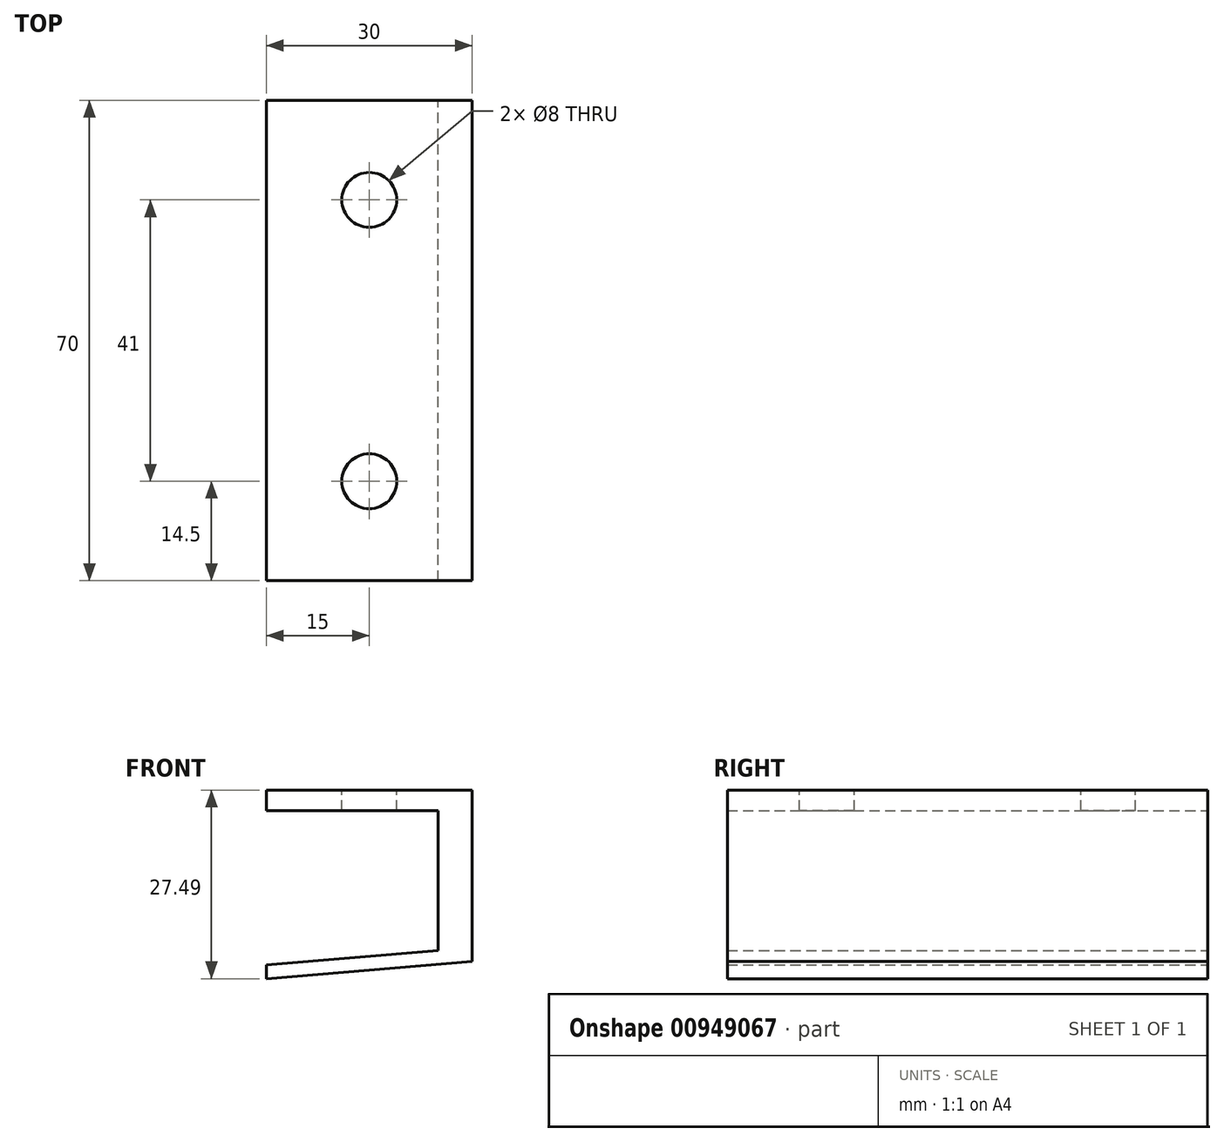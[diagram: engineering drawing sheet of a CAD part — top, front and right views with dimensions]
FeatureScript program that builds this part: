
annotation { "Feature Type Name" : "Feature", "Feature Type Description" : "" }
export const myFeature = defineFeature(function(context is Context, id is Id, definition is map)
    precondition{}
    {
        {
            var Q0;
            Q0=qCreatedBy(makeId("Front.planeOp"),FACE);
            var sketch = newSketch(context, id + "F0", { "sketchPlane" : qUnion([Q0])});
            skLineSegment(sketch, "E0", {"start": v(0, 0) * mm, "end": v(0, 3) * mm});
            skLineSegment(sketch, "E1", {"start": v(0, 3) * mm, "end": v(30, 3) * mm});
            skLineSegment(sketch, "E2", {"start": v(30, 3) * mm, "end": v(30, -22) * mm});
            skLineSegment(sketch, "E3", {"start": v(0, 0) * mm, "end": v(25, 0) * mm});
            skLineSegment(sketch, "E4", {"start": v(25, -23.46) * mm, "end": v(25, 0) * mm});
            skLineSegment(sketch, "E5", {"start": v(30, -22) * mm, "end": v(0, -24.5) * mm});
            skLineSegment(sketch, "E6", {"start": v(0, -24.5) * mm, "end": v(0, -22.5) * mm});
            skLineSegment(sketch, "E7", {"start": v(0, -22.5) * mm, "end": v(25, -20.42) * mm});
            skLineSegment(sketch, "E8", {"start": v(25, -23.46) * mm, "end": v(25, -20.42) * mm});
            skSolve(sketch);
        }
        {
            var Q0;
            Q0 = qSketchRegion(id + "F0", true);
            extrude(context, id + "F1", {"entities" : qUnion([Q0]), "depth" : 70 * mm, "offsetDistance" : 25 * mm});
        }
        {
            var Q0;
            Q0=makeQuery(id+"F1.opExtrude","SWEPT_FACE",FACE,{"disambiguationData":[OSD([sQuery(id+"F0.wireOp",EDGE,"E1")])]});
            var sketch = newSketch(context, id + "F2", { "sketchPlane" : qUnion([Q0])});
            skLineSegment(sketch, "E9", {"start": v(15, 0) * mm, "end": v(15, -14.5) * mm});
            skLineSegment(sketch, "E10", {"start": v(15, -14.5) * mm, "end": v(15, -55.5) * mm});
            skCircle(sketch, "E11", {"center": v(15, -14.5) * mm, "radius": 4 * mm});
            skCircle(sketch, "E12", {"center": v(15, -55.5) * mm, "radius": 4 * mm});
            skSolve(sketch);
        }
        {
            var Q0;
            Q0 = qSketchRegion(id + "F2", true);
            extrude(context, id + "F3", {"entities" : qUnion([Q0]), "operationType" : NewBodyOperationType.REMOVE, "oppositeDirection" : true, "depth" : 5 * mm, "offsetDistance" : 25 * mm});
        }
    });
